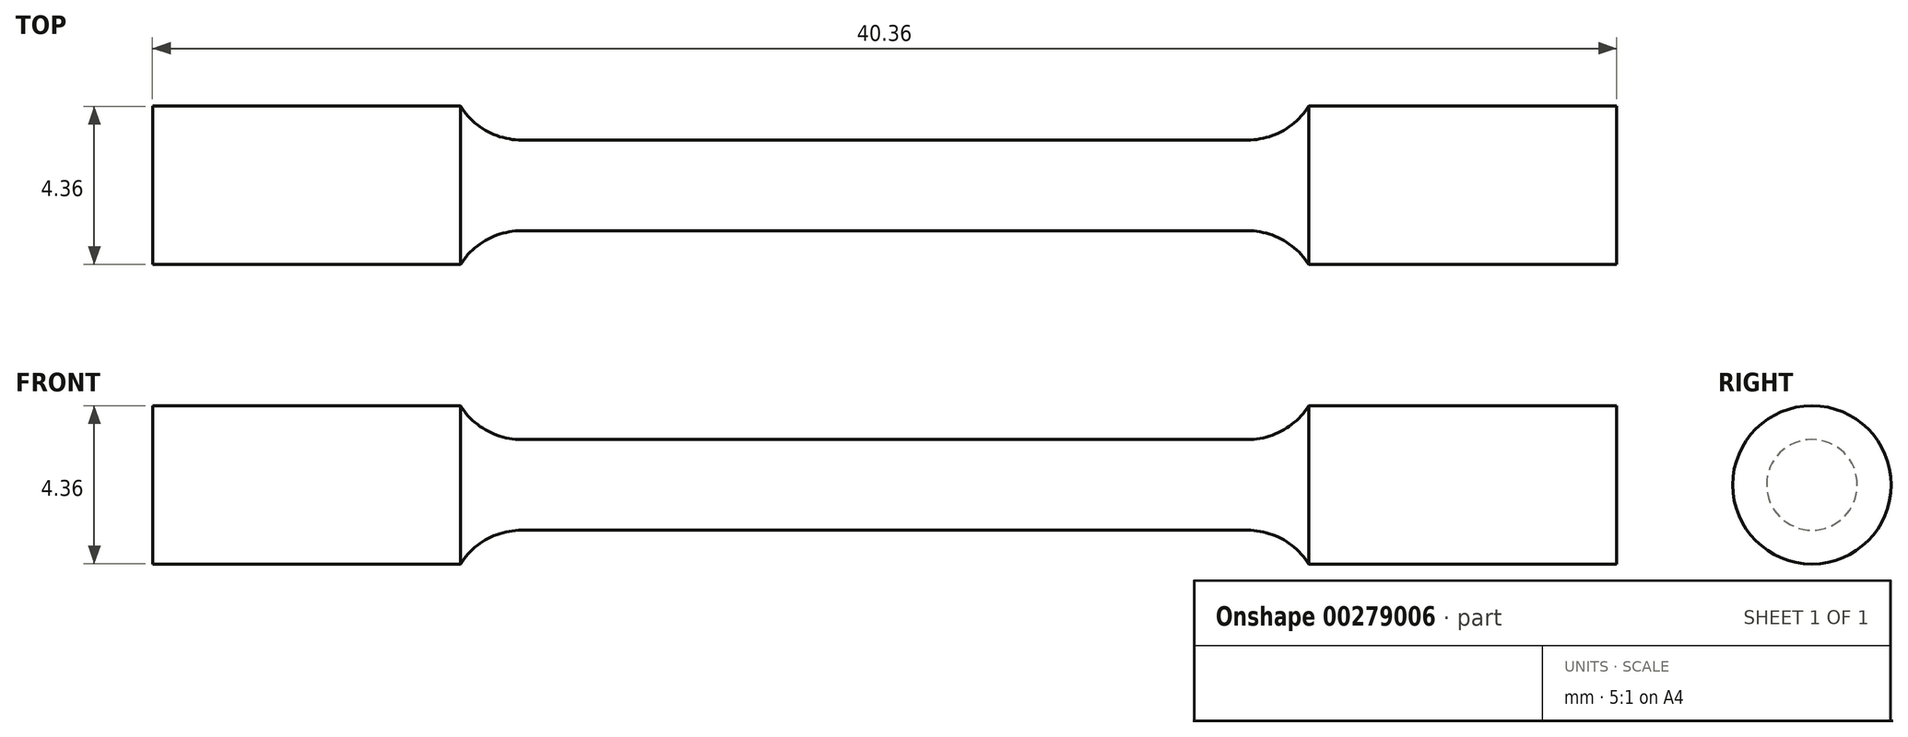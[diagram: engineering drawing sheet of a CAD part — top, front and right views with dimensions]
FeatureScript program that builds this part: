
annotation { "Feature Type Name" : "Feature", "Feature Type Description" : "" }
export const myFeature = defineFeature(function(context is Context, id is Id, definition is map)
    precondition{}
    {
        {
            var Q0;
            Q0=qCreatedBy(makeId("Front.planeOp"),FACE);
            var sketch = newSketch(context, id + "F0", { "sketchPlane" : qUnion([Q0])});
            skLineSegment(sketch, "E0", {"start": v(0, 1.25) * mm, "end": v(10, 1.25) * mm});
            skArc(sketch, "E1", {"start": v(10, 1.25) * mm, "mid": v(10.97, 1.5) * mm, "end": v(11.7, 2.18) * mm});
            skLineSegment(sketch, "E2", {"start": v(11.7, 2.18) * mm, "end": v(20.18, 2.18) * mm});
            skLineSegment(sketch, "E3", {"start": v(20.18, 2.18) * mm, "end": v(20.18, 0) * mm});
            skLineSegment(sketch, "E4.MirrorCS", {"start": v(0, 1.25) * mm, "end": v(-10, 1.25) * mm});
            skLineSegment(sketch, "E5.MirrorCS", {"start": v(-20.18, 2.18) * mm, "end": v(-20.18, 0) * mm});
            skLineSegment(sketch, "E6.MirrorCS", {"start": v(-11.7, 2.18) * mm, "end": v(-20.18, 2.18) * mm});
            skArc(sketch, "E7.MirrorCS", {"start": v(-10, 1.25) * mm, "mid": v(-10.97, 1.5) * mm, "end": v(-11.7, 2.18) * mm});
            skLineSegment(sketch, "E8", {"start": v(-20.18, 0) * mm, "end": v(20.18, 0) * mm});
            skSolve(sketch);
        }
        {
            var Q0;
            Q0=makeQuery(id+"F0.imprint","IMPRINT",FACE,{"disambiguationData":[TD([[makeQuery(id+"F0.imprint","IMPRINT",EDGE,{"derivedFrom":sQuery(id+"F0.wireOp",EDGE,"E0")}),-1.0]])]});
            var Q1;
            Q1=sQuery(id+"F0.wireOp",EDGE,"E8");
            revolve(context, id + "F1", {"entities" : qUnion([Q0]), "axis" : qUnion([Q1]), "revolveType" : RevolveType.FULL});
        }
    });
